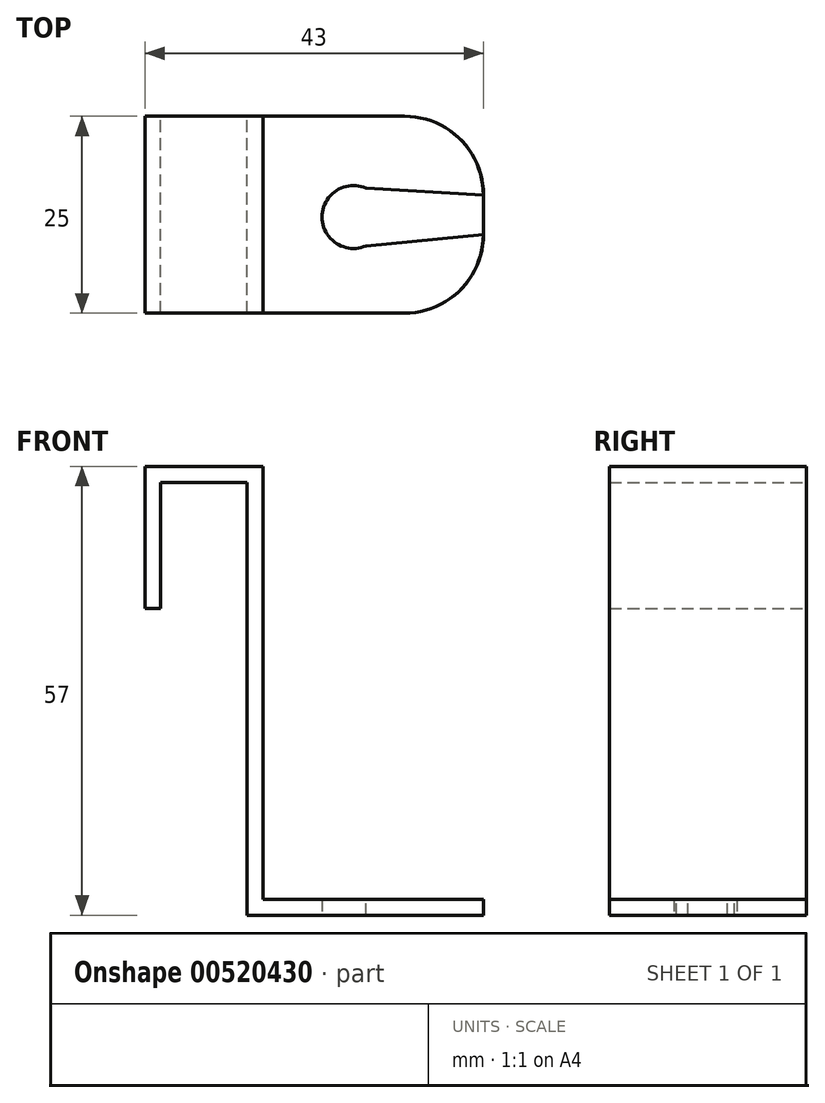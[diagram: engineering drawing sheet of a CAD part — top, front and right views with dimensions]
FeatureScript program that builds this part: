
annotation { "Feature Type Name" : "Feature", "Feature Type Description" : "" }
export const myFeature = defineFeature(function(context is Context, id is Id, definition is map)
    precondition{}
    {
        {
            var Q0;
            Q0=qCreatedBy(makeId("Front.planeOp"),FACE);
            var sketch = newSketch(context, id + "F0", { "sketchPlane" : qUnion([Q0])});
            skLineSegment(sketch, "E0", {"start": v(0, 0) * mm, "end": v(0, 55) * mm});
            skLineSegment(sketch, "E1", {"start": v(0, 55) * mm, "end": v(-11, 55) * mm});
            skLineSegment(sketch, "E2", {"start": v(-11, 55) * mm, "end": v(-11, 39) * mm});
            skLineSegment(sketch, "E3", {"start": v(0, 0) * mm, "end": v(30, 0) * mm});
            skLineSegment(sketch, "E4", {"start": v(-11, 39) * mm, "end": v(-13, 39) * mm});
            skLineSegment(sketch, "E5", {"start": v(-13, 39) * mm, "end": v(-13, 57) * mm});
            skLineSegment(sketch, "E6", {"start": v(-13, 57) * mm, "end": v(2, 57) * mm});
            skLineSegment(sketch, "E7", {"start": v(2, 57) * mm, "end": v(2, 2) * mm});
            skLineSegment(sketch, "E8", {"start": v(2, 2) * mm, "end": v(29.98, 2) * mm});
            skLineSegment(sketch, "E9", {"start": v(29.98, 2) * mm, "end": v(30, 0) * mm});
            skSolve(sketch);
        }
        {
            var Q0;
            Q0 = qSketchRegion(id + "F0", true);
            extrude(context, id + "F1", {"entities" : qUnion([Q0]), "depth" : 25 * mm, "offsetDistance" : 25 * mm});
        }
        {
            var Q0;
            Q0=makeQuery(id+"F1.opExtrude","SWEPT_FACE",FACE,{"disambiguationData":[OSD([sQuery(id+"F0.wireOp",EDGE,"E3")])]});
            var sketch = newSketch(context, id + "F2", { "sketchPlane" : qUnion([Q0])});
            skPoint(sketch, "E10", {"position": v(13.5, 12.8) * mm});
            skSolve(sketch);
        }
        {
            var Q0;
            Q0=sQuery(id+"F2.wireOp",VERTEX,"E10");
            var Q1;
            Q1=makeQuery(id+"F1.opExtrude","SWEPT_BODY",BODY,{"disambiguationData":[OSD([sQuery(id+"F0.wireOp",EDGE,"E0"),sQuery(id+"F0.wireOp",EDGE,"E1"),sQuery(id+"F0.wireOp",EDGE,"E2"),sQuery(id+"F0.wireOp",EDGE,"E3"),sQuery(id+"F0.wireOp",EDGE,"E4"),sQuery(id+"F0.wireOp",EDGE,"E5"),sQuery(id+"F0.wireOp",EDGE,"E6"),sQuery(id+"F0.wireOp",EDGE,"E7"),sQuery(id+"F0.wireOp",EDGE,"E8"),sQuery(id+"F0.wireOp",EDGE,"E9")])]});
            hole(context, id + "F3", {"style" : HoleStyle.C_SINK, "endStyle" : HoleEndStyle.BLIND, "holeDiameter" : 8 * mm, "cSinkDiameter" : 8 * mm, "cSinkAngle" : 45 * degree, "holeDepth" : 20 * mm, "isTappedThrough" : true, "tappedDepth" : 12 * mm, "tapClearance" : 3, "locations" : qUnion([Q0]), "scope" : qUnion([Q1])});
        }
        {
            var Q0;
            Q0=makeQuery(id+"F1.opExtrude","CAP_EDGE",EDGE,{"disambiguationData":[OSD([sQuery(id+"F0.wireOp",EDGE,"E9")])],"isStart":true});
            var Q1;
            Q1=makeQuery(id+"F1.opExtrude","CAP_EDGE",EDGE,{"disambiguationData":[OSD([sQuery(id+"F0.wireOp",EDGE,"E9")])],"isStart":false});
            fillet(context, id + "F4", {"entities" : qUnion([Q0, Q1]), "radius" : 10 * mm, "tangentPropagation" : true, "allowEdgeOverflow" : false});
        }
        {
            var Q0;
            Q0=makeQuery(id+"F1.opExtrude","SWEPT_FACE",FACE,{"disambiguationData":[OSD([sQuery(id+"F0.wireOp",EDGE,"E8")])]});
            var sketch = newSketch(context, id + "F5", { "sketchPlane" : qUnion([Q0])});
            skLineSegment(sketch, "E11", {"start": v(29.98, -10) * mm, "end": v(15.1, -9.13) * mm});
            skLineSegment(sketch, "E12", {"start": v(15.1, -9.13) * mm, "end": v(15.1, -16.46) * mm});
            skLineSegment(sketch, "E13", {"start": v(15.1, -16.46) * mm, "end": v(29.98, -15) * mm});
            skLineSegment(sketch, "E14", {"start": v(29.98, -15) * mm, "end": v(29.98, -10) * mm});
            skSolve(sketch);
        }
        {
            var Q0;
            Q0 = qSketchRegion(id + "F5", true);
            extrude(context, id + "F6", {"entities" : qUnion([Q0]), "operationType" : NewBodyOperationType.REMOVE, "endBound" : BoundingType.THROUGH_ALL, "oppositeDirection" : true, "depth" : 25 * mm, "offsetDistance" : 25 * mm});
        }
    });
